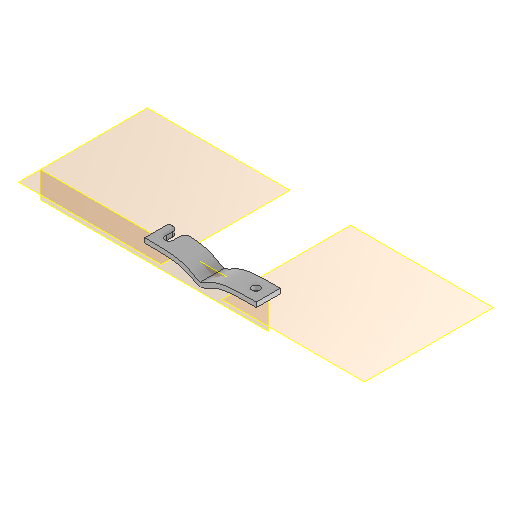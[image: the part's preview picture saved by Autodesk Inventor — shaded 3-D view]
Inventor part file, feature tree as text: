
AUTODESK INVENTOR PART (.ipt)
format: ipt  version: 2024.1 (Build 281209000, 209)  size: 182,272 bytes
history: native  units: mm
features: plane x3, extrude x3, sketch x3, other x2, mirror x1, fillet x1, reference x1
ambient origin geometry x8: Origin, YZ Plane, XZ Plane, XY Plane, X Axis, Y Axis, Z Axis, Center Point
bodies: Volumenkörper1 (feature_tree)
feature tree (14):
  plane  "Arbeitsebene1"
  extrude  "Extrusion1"  Depth=10.0mm
  plane  "Arbeitsebene2"
  extrude  "Extrusion2"  Depth=10.0mm TaperAngle=0.0deg
  mirror  "Spiegeln1"
  extrude  "Extrusion3"  [1 undecoded]
  fillet  "Rundung1"  [1 undecoded]
  sketch  "Skizze1"  dims[d0=10.0mm d1=0.0mm d2=3.2mm]
  sketch  "Skizze2"  dims[d3=10.0mm d4=0.0mm d5=10.0mm d6=0.0mm]
  reference  "Referenz2"
  plane  "Arbeitsebene3"
  sketch  "Skizze3"  dims[d7=2.0mm]
  other  "Assembly_Planktoscope_Uc2version_wormdrive_V3.iam"
  other  "60_Planktoscope_Sampleholder:1"
note: 2 required parameter values undecoded (feature->parameter linkage not recoverable at this tier; creation-order binding heuristic only, values carry confidence <= 0.55)
